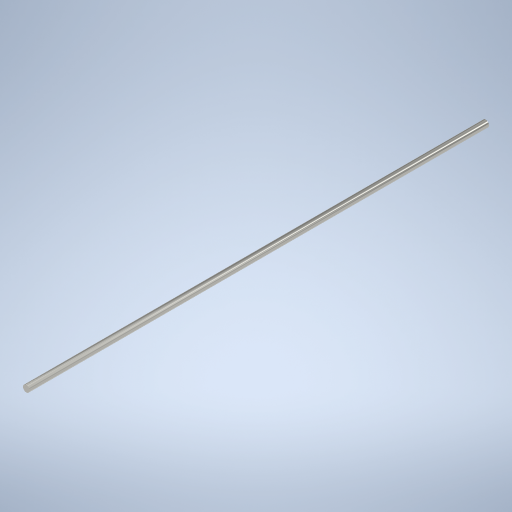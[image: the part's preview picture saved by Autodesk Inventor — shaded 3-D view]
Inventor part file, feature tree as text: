
AUTODESK INVENTOR PART (.ipt)
format: ipt  version: 2024.2 (Build 282272000, 272)  size: 246,784 bytes
history: native  units: mm
features: other x2, extrude x1, sketch x1
ambient origin geometry x8: Origin, YZ Plane, XZ Plane, XY Plane, X Axis, Y Axis, Z Axis, Center Point
bodies: Body1 (feature_tree)
feature tree (4):
  other  "Bryła1"
  extrude  "Wyciągnięcie proste1"  Depth=6.0mm
  sketch  "Szkic1"
  other  "Finish1"
